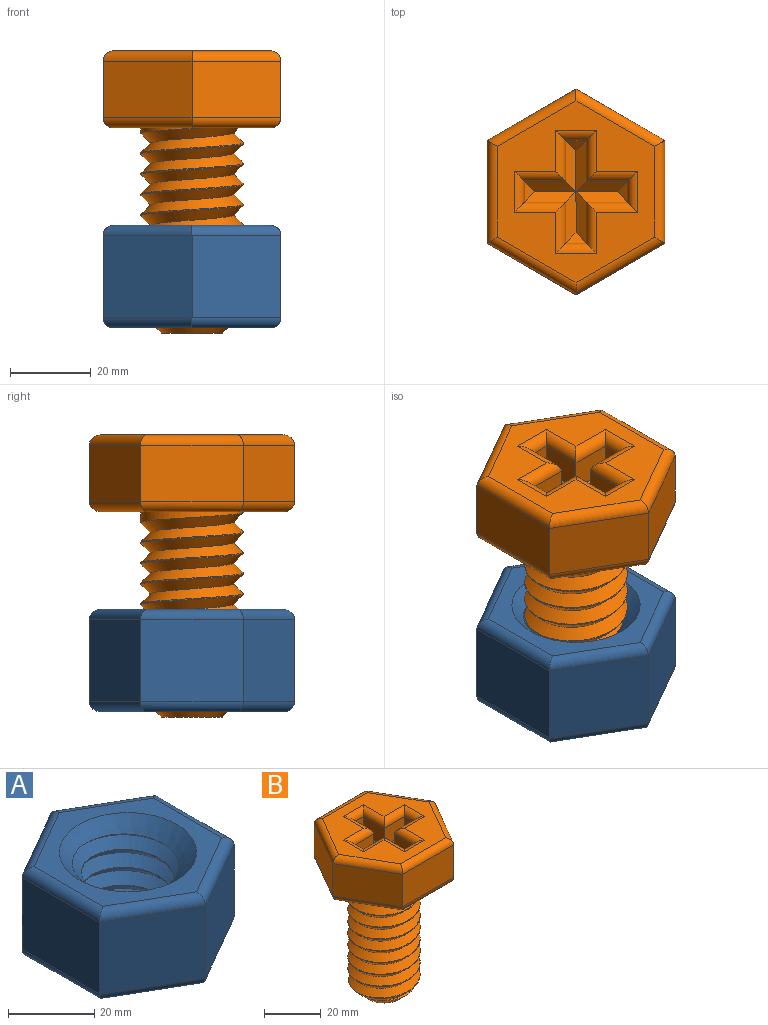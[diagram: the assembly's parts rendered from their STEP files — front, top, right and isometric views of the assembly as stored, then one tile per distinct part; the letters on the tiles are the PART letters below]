
ASSEMBLY  parts=2 mates=1
PART A: 25 faces, bbox 44x50.8x25.4 mm
  f0: plane 44.93x38.91mm, normal (0,0,-1), area 519.7mm2, adj f12,f13,f14,f15,f16,f17,f18
  f1: plane 22x20.32mm, normal (0.5,0.87,0), area 516.1mm2, adj f2,f6,f16,f22
  f2: plane 22x20.32mm, normal (-0.5,0.87,0), area 516.1mm2, adj f1,f3,f14,f20
  f3: plane 25.4x20.32mm, normal (-1,0,0), area 516.1mm2, adj f2,f4,f13,f19
  f4: plane 22x20.32mm, normal (-0.5,-0.87,0), area 516.1mm2, adj f3,f5,f15,f21
  f5: plane 22x20.32mm, normal (0.5,-0.87,0), area 516.1mm2, adj f4,f6,f17,f23
  f6: plane 25.4x20.32mm, normal (1,0,0), area 516.1mm2, adj f1,f5,f18,f24
  f7: cylinder r=10.79mm len=21.59mm, axis (0,0,-1), area 51.9mm2, adj f9,f10,f11,f12
  f8: plane 44.93x38.91mm, normal (0,0,1), area 519.7mm2, adj f11,f19,f20,f21,f22,f23,f24
  f9: bspline ~30.5x26.42mm, area 899.1mm2, adj f7,f10,f11,f12
  f10: bspline ~30.5x26.42mm, area 899.6mm2, adj f7,f9,f11,f12
  f11: cone r=10.79mm half-angle=45deg, axis (0,0,1), area 484.2mm2, adj f7,f8,f9,f10
  f12: cone r=15.88mm half-angle=45deg, axis (0,0,-1), area 484.2mm2, adj f0,f7,f9,f10
  f13: cylinder r=2.54mm len=25.4mm, axis (0,-1,0), area 95.5mm2, adj f0,f3,f14,f15
  f14: cylinder r=2.54mm len=23.27mm, axis (-0.87,-0.5,0), area 95.5mm2, adj f0,f2,f13,f16
  f15: cylinder r=2.54mm len=23.27mm, axis (0.87,-0.5,0), area 95.5mm2, adj f0,f4,f13,f17
  f16: cylinder r=2.54mm len=23.27mm, axis (-0.87,0.5,0), area 95.5mm2, adj f0,f1,f14,f18
  f17: cylinder r=2.54mm len=23.27mm, axis (0.87,0.5,0), area 95.5mm2, adj f0,f5,f15,f18
  f18: cylinder r=2.54mm len=25.4mm, axis (0,1,0), area 95.5mm2, adj f0,f6,f16,f17
  f19: cylinder r=2.54mm len=25.4mm, axis (0,1,0), area 95.5mm2, adj f3,f8,f20,f21
  f20: cylinder r=2.54mm len=23.27mm, axis (0.87,0.5,0), area 95.5mm2, adj f2,f8,f19,f22
  f21: cylinder r=2.54mm len=23.27mm, axis (-0.87,0.5,0), area 95.5mm2, adj f4,f8,f19,f23
  f22: cylinder r=2.54mm len=23.27mm, axis (0.87,-0.5,0), area 95.5mm2, adj f1,f8,f20,f24
  f23: cylinder r=2.54mm len=23.27mm, axis (-0.87,-0.5,0), area 95.5mm2, adj f5,f8,f21,f24
  f24: cylinder r=2.54mm len=25.4mm, axis (0,-1,0), area 95.5mm2, adj f6,f8,f22,f23
PART B: 63 faces, bbox 50.8x44x69.9 mm
  f0: cylinder r=12.7mm len=45.72mm, axis (0,0,-1), area 31.4mm2, adj f9,f58,f60,f61,f62
  f1: plane 44.93x38.91mm, normal (0,0,1), area 795.3mm2, adj f34,f35,f36,f37,f38,f39,f40,f41
  f2: plane 15.24x15.24mm, normal (0,0,-1), area 182.4mm2, adj f62
  f3: plane 22x13.97mm, normal (0.87,0.5,0), area 354.8mm2, adj f4,f8,f47,f53
  f4: plane 25.4x13.97mm, normal (0,1,0), area 354.8mm2, adj f3,f5,f46,f52
  f5: plane 22x13.97mm, normal (-0.87,0.5,0), area 354.8mm2, adj f4,f6,f48,f54
  f6: plane 22x13.97mm, normal (-0.87,-0.5,0), area 354.8mm2, adj f5,f7,f50,f56
  f7: plane 25.4x13.97mm, normal (0,-1,0), area 354.8mm2, adj f6,f8,f51,f57
  f8: plane 22x13.97mm, normal (0.87,-0.5,0), area 354.8mm2, adj f3,f7,f49,f55
  f9: plane 44.93x38.91mm, normal (0,0,-1), area 804.7mm2, adj f0,f46,f47,f48,f49,f50,f51,f59
  f10: plane 10.16x7.62mm, normal (0,-1,0), area 77.4mm2, adj f11,f21,f31,f43
  f11: plane 10.16x7.62mm, normal (-1,0,0), area 77.4mm2, adj f10,f12,f29,f45
  f12: plane 7.62x5.08mm, normal (0,-1,0), area 38.7mm2, adj f11,f13,f26,f44
  f13: plane 10.16x7.62mm, normal (1,0,0), area 77.4mm2, adj f12,f14,f25,f42
  f14: plane 10.16x7.62mm, normal (0,-1,0), area 77.4mm2, adj f13,f15,f23,f40
  f15: plane 7.62x5.08mm, normal (1,0,0), area 38.7mm2, adj f14,f16,f22,f38
  f16: plane 10.16x7.62mm, normal (0,1,0), area 77.4mm2, adj f15,f17,f24,f36
  f17: plane 10.16x7.62mm, normal (1,0,0), area 77.4mm2, adj f16,f18,f28,f34
  f18: plane 7.62x5.08mm, normal (0,1,0), area 38.7mm2, adj f17,f19,f27,f35
  f19: plane 10.16x7.62mm, normal (-1,0,0), area 77.4mm2, adj f18,f20,f30,f37
  f20: plane 10.16x7.62mm, normal (0,1,0), area 77.4mm2, adj f19,f21,f33,f39
  f21: plane 7.62x5.08mm, normal (-1,0,0), area 38.7mm2, adj f10,f20,f32,f41
  f22: plane 5.08x2.54mm, normal (0.71,0,0.71), area 9.1mm2, adj f15,f23,f24
  f23: plane 12.7x2.54mm, normal (0,-0.71,0.71), area 36.5mm2, adj f14,f22,f24,f25
  f24: plane 12.7x2.54mm, normal (0,0.71,0.71), area 36.5mm2, adj f16,f22,f23,f28
  f25: plane 12.7x2.54mm, normal (0.71,0,0.71), area 36.5mm2, adj f13,f23,f26,f29
  f26: plane 5.08x2.54mm, normal (0,-0.71,0.71), area 9.1mm2, adj f12,f25,f29
  f27: plane 5.08x2.54mm, normal (0,0.71,0.71), area 9.1mm2, adj f18,f28,f30
  f28: plane 12.7x2.54mm, normal (0.71,0,0.71), area 36.5mm2, adj f17,f24,f27,f30
  f29: plane 12.7x2.54mm, normal (-0.71,0,0.71), area 36.5mm2, adj f11,f25,f26,f31
  f30: plane 12.7x2.54mm, normal (-0.71,0,0.71), area 36.5mm2, adj f19,f27,f28,f33
  f31: plane 12.7x2.54mm, normal (0,-0.71,0.71), area 36.5mm2, adj f10,f29,f32,f33
  f32: plane 5.08x2.54mm, normal (-0.71,0,0.71), area 9.1mm2, adj f21,f31,f33
  f33: plane 12.7x2.54mm, normal (0,0.71,0.71), area 36.5mm2, adj f20,f30,f31,f32
  f34: cylinder r=2.54mm len=12.7mm, axis (0,1,0), area 40.5mm2, adj f1,f17,f35,f36
  f35: cylinder r=2.54mm len=10.16mm, axis (-1,0,0), area 30.4mm2, adj f1,f18,f34,f37
  f36: cylinder r=2.54mm len=12.7mm, axis (-1,0,0), area 40.5mm2, adj f1,f16,f34,f38
  f37: cylinder r=2.54mm len=12.7mm, axis (0,-1,0), area 40.5mm2, adj f1,f19,f35,f39
  f38: cylinder r=2.54mm len=10.16mm, axis (0,1,0), area 30.4mm2, adj f1,f15,f36,f40
  f39: cylinder r=2.54mm len=12.7mm, axis (-1,0,0), area 40.5mm2, adj f1,f20,f37,f41
  f40: cylinder r=2.54mm len=12.7mm, axis (1,0,0), area 40.5mm2, adj f1,f14,f38,f42
  f41: cylinder r=2.54mm len=10.16mm, axis (0,-1,0), area 30.4mm2, adj f1,f21,f39,f43
  f42: cylinder r=2.54mm len=12.7mm, axis (0,1,0), area 40.5mm2, adj f1,f13,f40,f44
  f43: cylinder r=2.54mm len=12.7mm, axis (1,0,0), area 40.5mm2, adj f1,f10,f41,f45
  f44: cylinder r=2.54mm len=10.16mm, axis (1,0,0), area 30.4mm2, adj f1,f12,f42,f45
  f45: cylinder r=2.54mm len=12.7mm, axis (0,-1,0), area 40.5mm2, adj f1,f11,f43,f44
  f46: cylinder r=2.54mm len=25.4mm, axis (-1,0,0), area 95.5mm2, adj f4,f9,f47,f48
  f47: cylinder r=2.54mm len=23.27mm, axis (-0.5,0.87,0), area 95.5mm2, adj f3,f9,f46,f49
  f48: cylinder r=2.54mm len=23.27mm, axis (-0.5,-0.87,0), area 95.5mm2, adj f5,f9,f46,f50
  f49: cylinder r=2.54mm len=23.27mm, axis (0.5,0.87,0), area 95.5mm2, adj f8,f9,f47,f51
  f50: cylinder r=2.54mm len=23.27mm, axis (0.5,-0.87,0), area 95.5mm2, adj f6,f9,f48,f51
  f51: cylinder r=2.54mm len=25.4mm, axis (1,0,0), area 95.5mm2, adj f7,f9,f49,f50
  f52: cylinder r=2.54mm len=25.4mm, axis (1,0,0), area 95.5mm2, adj f1,f4,f53,f54
  f53: cylinder r=2.54mm len=23.27mm, axis (0.5,-0.87,0), area 95.5mm2, adj f1,f3,f52,f55
  f54: cylinder r=2.54mm len=23.27mm, axis (0.5,0.87,0), area 95.5mm2, adj f1,f5,f52,f56
  f55: cylinder r=2.54mm len=23.27mm, axis (-0.5,-0.87,0), area 95.5mm2, adj f1,f8,f53,f57
  f56: cylinder r=2.54mm len=23.27mm, axis (-0.5,0.87,0), area 95.5mm2, adj f1,f6,f54,f57
  f57: cylinder r=2.54mm len=25.4mm, axis (-1,0,0), area 95.5mm2, adj f1,f7,f55,f56
  f58: bspline ~50.67x29.33mm, area 2212.1mm2, adj f0,f60,f61,f62
  f59: cylinder r=12.7mm len=25.23mm, axis (0,0,-1), area 45.6mm2, adj f9,f60,f61
  f60: plane 4.83x2.41mm, normal (0,-1,0), area 5.8mm2, adj f0,f58,f59,f61
  f61: bspline ~50.67x29.33mm, area 2330.9mm2, adj f0,f58,f59,f60,f62
  f62: cone r=12.7mm half-angle=45deg, axis (0,0,1), area 337.8mm2, adj f0,f2,f58,f61
PLACE A t=(0,0,-11.43)mm
PLACE B rot(axis=(0,0,1),90deg) t=(0,0,0)mm
MATE cylindrical A.f7 <-> B.f0  axis (0,0,-1) through (0,0,-24.13)mm
